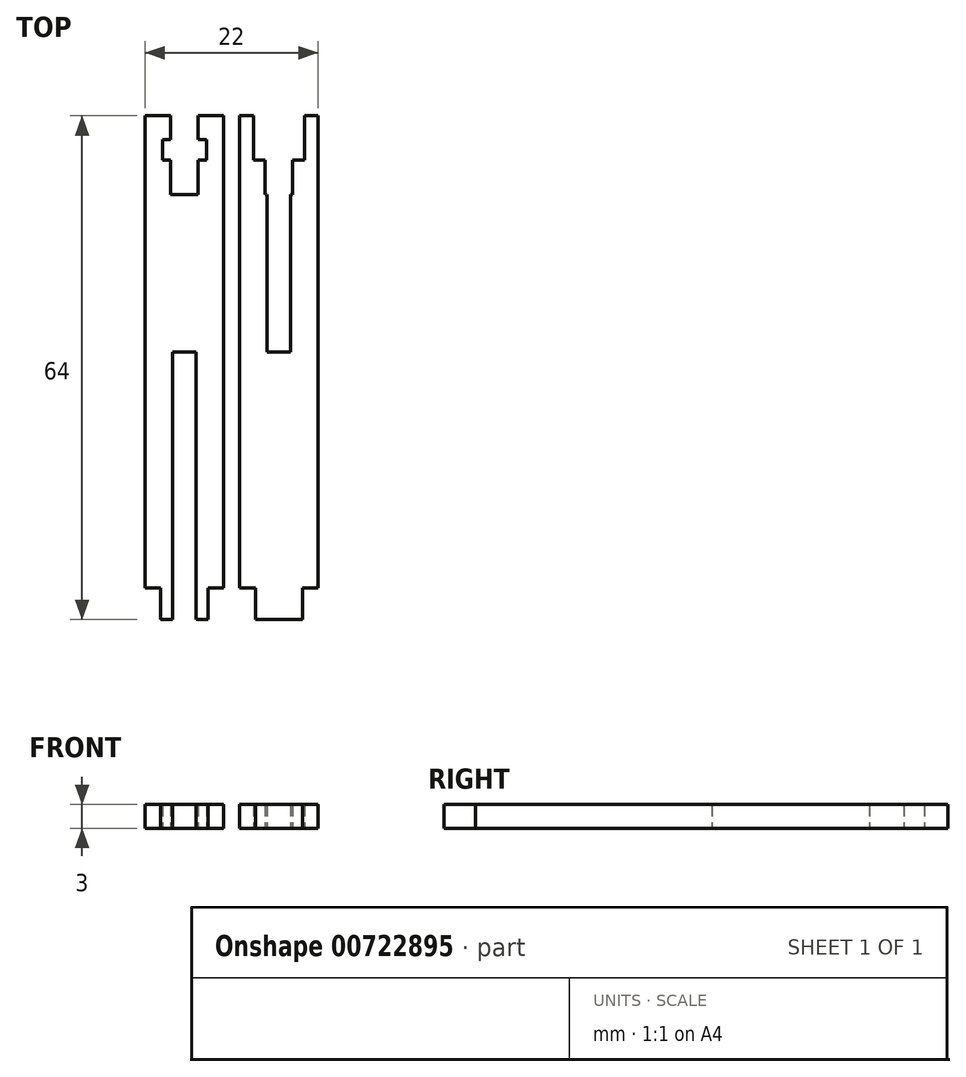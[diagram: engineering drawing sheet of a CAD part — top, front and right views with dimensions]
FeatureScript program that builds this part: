
annotation { "Feature Type Name" : "Feature", "Feature Type Description" : "" }
export const myFeature = defineFeature(function(context is Context, id is Id, definition is map)
    precondition{}
    {
        {
            var Q0;
            Q0=qCreatedBy(makeId("Top.planeOp"),FACE);
            var sketch = newSketch(context, id + "F0", { "sketchPlane" : qUnion([Q0])});
            skLineSegment(sketch, "E0", {"start": v(-11, 32) * mm, "end": v(-7.75, 32) * mm});
            skLineSegment(sketch, "E1", {"start": v(-7.75, 32) * mm, "end": v(-7.75, 29) * mm});
            skLineSegment(sketch, "E2", {"start": v(-7.75, 29) * mm, "end": v(-8.8, 29) * mm});
            skLineSegment(sketch, "E3", {"start": v(-8.8, 29) * mm, "end": v(-8.8, 26.4) * mm});
            skLineSegment(sketch, "E4", {"start": v(-8.8, 26.4) * mm, "end": v(-7.75, 26.4) * mm});
            skLineSegment(sketch, "E5", {"start": v(-7.75, 26.4) * mm, "end": v(-7.75, 22) * mm});
            skLineSegment(sketch, "E6", {"start": v(-7.75, 22) * mm, "end": v(-4.25, 22) * mm});
            skLineSegment(sketch, "E7", {"start": v(-4.25, 22) * mm, "end": v(-4.25, 26.4) * mm});
            skLineSegment(sketch, "E8", {"start": v(-4.25, 26.4) * mm, "end": v(-3.2, 26.4) * mm});
            skLineSegment(sketch, "E9", {"start": v(-3.2, 26.4) * mm, "end": v(-3.2, 29) * mm});
            skLineSegment(sketch, "E10", {"start": v(-3.2, 29) * mm, "end": v(-4.25, 29) * mm});
            skLineSegment(sketch, "E11", {"start": v(-4.25, 29) * mm, "end": v(-4.25, 32) * mm});
            skLineSegment(sketch, "E12", {"start": v(-4.25, 32) * mm, "end": v(-1, 32) * mm});
            skLineSegment(sketch, "E13", {"start": v(-1, 32) * mm, "end": v(-1, -28) * mm});
            skLineSegment(sketch, "E14", {"start": v(-1, -28) * mm, "end": v(-3, -28) * mm});
            skLineSegment(sketch, "E15", {"start": v(-3, -28) * mm, "end": v(-3, -32) * mm});
            skLineSegment(sketch, "E16", {"start": v(-3, -32) * mm, "end": v(-4.5, -32) * mm});
            skLineSegment(sketch, "E17", {"start": v(-4.5, -32) * mm, "end": v(-4.5, 2) * mm});
            skLineSegment(sketch, "E18", {"start": v(-4.5, 2) * mm, "end": v(-7.5, 2) * mm});
            skLineSegment(sketch, "E19", {"start": v(-7.5, 2) * mm, "end": v(-7.5, -32) * mm});
            skLineSegment(sketch, "E20", {"start": v(-7.5, -32) * mm, "end": v(-9, -32) * mm});
            skLineSegment(sketch, "E21", {"start": v(-9, -32) * mm, "end": v(-9, -28) * mm});
            skLineSegment(sketch, "E22", {"start": v(-9, -28) * mm, "end": v(-11, -28) * mm});
            skLineSegment(sketch, "E23", {"start": v(-11, -28) * mm, "end": v(-11, 32) * mm});
            skLineSegment(sketch, "E24", {"start": v(1, 32) * mm, "end": v(2.75, 32) * mm});
            skLineSegment(sketch, "E25", {"start": v(2.75, 32) * mm, "end": v(2.75, 26.4) * mm});
            skLineSegment(sketch, "E26", {"start": v(2.75, 26.4) * mm, "end": v(4.25, 26.4) * mm});
            skLineSegment(sketch, "E27", {"start": v(4.25, 26.4) * mm, "end": v(4.25, 22) * mm});
            skLineSegment(sketch, "E28", {"start": v(4.25, 22) * mm, "end": v(4.5, 22) * mm});
            skLineSegment(sketch, "E29", {"start": v(4.5, 22) * mm, "end": v(4.5, 2) * mm});
            skLineSegment(sketch, "E30", {"start": v(4.5, 2) * mm, "end": v(7.5, 2) * mm});
            skLineSegment(sketch, "E31", {"start": v(7.5, 2) * mm, "end": v(7.5, 22) * mm});
            skLineSegment(sketch, "E32", {"start": v(7.5, 22) * mm, "end": v(7.75, 22) * mm});
            skLineSegment(sketch, "E33", {"start": v(7.75, 22) * mm, "end": v(7.75, 26.4) * mm});
            skLineSegment(sketch, "E34", {"start": v(7.75, 26.4) * mm, "end": v(9.25, 26.4) * mm});
            skLineSegment(sketch, "E35", {"start": v(9.25, 26.4) * mm, "end": v(9.25, 32) * mm});
            skLineSegment(sketch, "E36", {"start": v(9.25, 32) * mm, "end": v(11, 32) * mm});
            skLineSegment(sketch, "E37", {"start": v(11, 32) * mm, "end": v(11, -28) * mm});
            skLineSegment(sketch, "E38", {"start": v(11, -28) * mm, "end": v(9, -28) * mm});
            skLineSegment(sketch, "E39", {"start": v(9, -28) * mm, "end": v(9, -32) * mm});
            skLineSegment(sketch, "E40", {"start": v(9, -32) * mm, "end": v(3, -32) * mm});
            skLineSegment(sketch, "E41", {"start": v(3, -32) * mm, "end": v(3, -28) * mm});
            skLineSegment(sketch, "E42", {"start": v(3, -28) * mm, "end": v(1, -28) * mm});
            skLineSegment(sketch, "E43", {"start": v(1, -28) * mm, "end": v(1, 32) * mm});
            skSolve(sketch);
        }
        {
            var Q0;
            Q0=makeQuery(id+"F0.imprint","IMPRINT",FACE,{"disambiguationData":[TD([[makeQuery(id+"F0.imprint","IMPRINT",EDGE,{"derivedFrom":sQuery(id+"F0.wireOp",EDGE,"E0")}),-1.0]])]});
            var Q1;
            Q1=makeQuery(id+"F0.imprint","IMPRINT",FACE,{"disambiguationData":[TD([[makeQuery(id+"F0.imprint","IMPRINT",EDGE,{"derivedFrom":sQuery(id+"F0.wireOp",EDGE,"E24")}),-1.0]])]});
            extrude(context, id + "F1", {"entities" : qUnion([Q0, Q1]), "depth" : 3 * mm, "offsetDistance" : 25 * mm});
        }
    });
